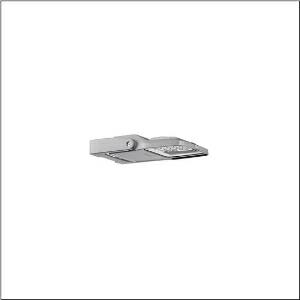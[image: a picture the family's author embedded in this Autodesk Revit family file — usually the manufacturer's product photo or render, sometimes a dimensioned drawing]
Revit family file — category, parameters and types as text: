
# Revit family: floodlight_fl_21_iq_micro___pl64_5xa7762a2e2a_90eb
name_source: partatom
category: Lighting Fixtures
units: mm (PartAtom-declared; Revit-internal decimal feet)

## family parameters
Cut with Voids When Loaded = No
Host = Face
Light Source = No
Part Type = Normal
Room Calculation Point = No
Round Connector Dimension = Use Diameter
Shared = No

## types (1)
- --- (1 x LED, 2870 lm, 23.1 W, 3000K)
    Apparent Load = 23 VA
    CIE Flux Codes = 28 80 98 100 100
    Color Rendering = 70
    Color Temperature = 3000K
    Default Elevation = 1800 mm
    Description = Floodlight FL 21 iQ micro, floodlight, primary light control with lens, of PMMA, primary optical cover: protective disc, of toughened safety glass, transparent, light distribution: PL64, light emission: direct distribution, installation type: surface-mounted, LED, High Power LED, rated luminous flux: 2.870lm, luminous efficacy: 124lm/W, light colour: 730, colour temperature: 3000K, control gear: iQ Street-Remote/DALI, control: Auto-Match, Temp-Guard, Night-Set, Smart-Wire, Desk-Remote (wireless, voltage-free reading and setting of iQ features in the workshop via application-optimized NFC function/RFID function), optimised constant luminous flux control (CLO 2.0), Street-Remote, with terminal, 6-pole, mains connection: 220..240V, AC, 50/60Hz, start of lifetime: 23W, end of service life: 24W, reduction: 11W, luminaire housing, of diecast aluminium, powder-coated, Siteco® metallic grey (DB 702S), corrosivity category C5 mid according to DIN EN ISO 12944, suitable for swimming pools, chlorine-resistant, sealing non-destructively replaceable, design bracket, of diecast aluminium, powder-coated, Siteco® metallic grey (DB 702S), protection rating (complete): IP66, insulation class (complete): insulation class II (safety insulation), certification: CE, ENEC, VDE, protection symbol: D, impact resistance: IK07, permissible operating ambient temperature: -40..+40°C, permissible operating ambient temperature for outdoor applications: -40..+50°C, standard: DIN EN 12944, LABS conformity tested according to VDMA 24364:2018-05, packaging unit: 1 piece

Light Distribution: PL64
    Height = 65 mm
    Lamp = 1 x LED
    Lamp Light Flux = 2870 lm
    Lamp Power = 23.1 W
    Lamp count = 1
    Length = 312 mm
    Luminous efficacy = 124 lm/W
    Manufacturer = Siteco
    ModVariant = No
    Model = 5XA7762A2E2A
    Mounting Place = Wall
    Mounting Type = Surface mounted
    Number of Poles = 1
    OnlyDefault = Yes
    Power Factor = 1
    Product Name = Floodlight FL 21 iQ micro | PL64
    Product group = floodlight | wall mounted
    ProductGroupID = 2001
    Protection Class = Protection class II
    Protection Degree = IP 66
    RLX_Detail_Level = 1
    RLX_Emergency_Light_Flux = 0 lm
    RLX_Emergency_Type = 0
    RLX_Emergency_Type_DB = No
    RlxData = <blob elided: 97577 chars, md5=b8596b2b>
    Socket = socket
    Standby Power = 0 W
    System Light Flux = 2870 lm
    System Power = 23 W
    Type Comments = factory setting: luminous flux: 100 % | dim-lin: 254 | 455 mA
    Type Image = l_1006878.jpg
    URL = http://relux.com
    VarID = @adj_180614
    Voltage = 0 V
    Weight = 0.00 kg
    Width = 230 mm

## geometry (parser evidence)
native form markers: Blend x4, Sweep x13
no freeform markers — native parametric forms only
